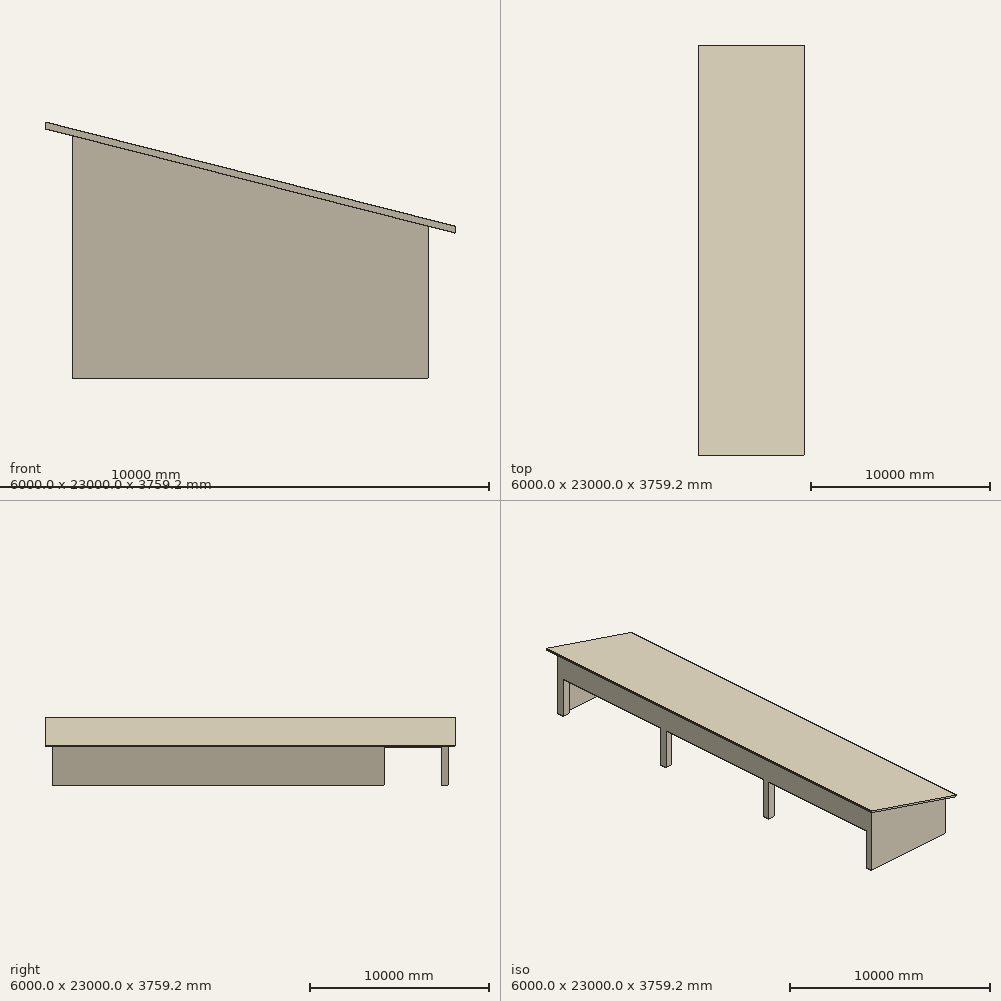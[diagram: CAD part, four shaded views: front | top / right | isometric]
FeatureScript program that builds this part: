
annotation { "Feature Type Name" : "Feature", "Feature Type Description" : "" }
export const myFeature = defineFeature(function(context is Context, id is Id, definition is map)
    precondition{}
    {
        {
            var Q0;
            Q0=qCreatedBy(makeId("Top.planeOp"),FACE);
            var sketch = newSketch(context, id + "F0", { "sketchPlane" : qUnion([Q0])});
            skLineSegment(sketch, "E0.bottom", {"start": v(0, 0) * mm, "end": v(-6000, 0) * mm});
            skLineSegment(sketch, "E0.top", {"start": v(0, 23000) * mm, "end": v(-6000, 23000) * mm});
            skLineSegment(sketch, "E0.left", {"start": v(0, 0) * mm, "end": v(0, 23000) * mm});
            skLineSegment(sketch, "E0.right", {"start": v(-6000, 0) * mm, "end": v(-6000, 23000) * mm});
            skSolve(sketch);
        }
        {
            var Q0;
            Q0=makeQuery(id+"F0.imprint","IMPRINT",FACE,{"disambiguationData":[TD([[makeQuery(id+"F0.imprint","IMPRINT",EDGE,{"derivedFrom":sQuery(id+"F0.wireOp",EDGE,"E0.bottom")}),-1.0]])]});
            extrude(context, id + "F1", {"entities" : qUnion([Q0]), "depth" : 3759.2 * mm, "offsetDistance" : 25 * mm});
        }
        {
            var Q0;
            Q0=makeQuery(id+"F1.opExtrude","SWEPT_FACE",FACE,{"disambiguationData":[OSD([sQuery(id+"F0.wireOp",EDGE,"E0.bottom")])]});
            var sketch = newSketch(context, id + "F2", { "sketchPlane" : qUnion([Q0])});
            skLineSegment(sketch, "E1", {"start": v(0, 0) * mm, "end": v(0, 2133.6) * mm});
            skLineSegment(sketch, "E2", {"start": v(0, 2133.6) * mm, "end": v(0, 2233.6) * mm});
            skLineSegment(sketch, "E3", {"start": v(0, 2233.6) * mm, "end": v(-6000, 3759.2) * mm});
            skLineSegment(sketch, "E4", {"start": v(-6000, 3759.2) * mm, "end": v(-6000, 3659.2) * mm});
            skLineSegment(sketch, "E5", {"start": v(-6000, 3659.2) * mm, "end": v(0, 2133.6) * mm});
            skLineSegment(sketch, "E6", {"start": v(0, 2133.6) * mm, "end": v(-6000, 2133.6) * mm});
            skLineSegment(sketch, "E7", {"start": v(0, 0) * mm, "end": v(-400, 0) * mm});
            skLineSegment(sketch, "E8", {"start": v(-400, 0) * mm, "end": v(-800, 0) * mm});
            skLineSegment(sketch, "E9", {"start": v(-800, 0) * mm, "end": v(-800, 2133.6) * mm});
            skLineSegment(sketch, "E10", {"start": v(-800, 2133.6) * mm, "end": v(-400, 2133.6) * mm});
            skLineSegment(sketch, "E11", {"start": v(-400, 2133.6) * mm, "end": v(-400, 0) * mm});
            skLineSegment(sketch, "E12", {"start": v(-6000, 0) * mm, "end": v(-5600, 0) * mm});
            skLineSegment(sketch, "E13", {"start": v(-5600, 0) * mm, "end": v(-5200, 0) * mm});
            skLineSegment(sketch, "E14", {"start": v(-5200, 0) * mm, "end": v(-5200, 2133.6) * mm});
            skLineSegment(sketch, "E15", {"start": v(-5200, 2133.6) * mm, "end": v(-5600, 2133.6) * mm});
            skLineSegment(sketch, "E16", {"start": v(-5600, 2133.6) * mm, "end": v(-5600, 0) * mm});
            skSolve(sketch);
        }
        {
            var Q0;
            {var subQ0=sQuery(id+"F2.wireOp",EDGE,"E9");Q0=makeQuery(id+"F2.imprint","IMPRINT",FACE,{"disambiguationData":[TD([[makeQuery(id+"F2.imprint","IMPRINT",EDGE,{"derivedFrom":subQ0}),1.0]])]});}
            var Q1;
            {var subQ0=sQuery(id+"F2.wireOp",EDGE,"E1");Q1=makeQuery(id+"F2.imprint","IMPRINT",FACE,{"disambiguationData":[TD([[makeQuery(id+"F2.imprint","IMPRINT",EDGE,{"derivedFrom":subQ0}),-1.0]])]});}
            var Q2;
            {var subQ4=sQuery(id+"F2.wireOp",EDGE,"E12");Q2=makeQuery(id+"F2.imprint","IMPRINT",FACE,{"disambiguationData":[TD([[makeQuery(id+"F2.imprint","IMPRINT",EDGE,{"derivedFrom":subQ4}),-1.0]])]});}
            var Q3;
            {var subQ0=sQuery(id+"F2.wireOp",EDGE,"E3");Q3=makeQuery(id+"F2.imprint","IMPRINT",FACE,{"disambiguationData":[TD([[makeQuery(id+"F2.imprint","IMPRINT",EDGE,{"derivedFrom":subQ0}),-1.0]])]});}
            extrude(context, id + "F3", {"entities" : qUnion([Q0, Q1, Q2, Q3]), "operationType" : NewBodyOperationType.REMOVE, "oppositeDirection" : true, "depth" : 22800 * mm, "offsetDistance" : 25 * mm});
        }
        {
            var Q0;
            Q0=makeQuery(id+"F3.boolean.opBoolean","COPY",FACE,{"derivedFrom":makeQuery(id+"F3.opExtrude","CAP_FACE",FACE,{"disambiguationData":[OSD([sQuery(id+"F0.wireOp",EDGE,"E0.bottom"),sQuery(id+"F0.wireOp",EDGE,"E0.left"),sQuery(id+"F2.wireOp",EDGE,"E3")])],"isStart":false})});
            var Q1;
            Q1=makeQuery(id+"F3.boolean.opBoolean","COPY",FACE,{"derivedFrom":makeQuery(id+"F3.opExtrude","CAP_FACE",FACE,{"disambiguationData":[OSD([sQuery(id+"F0.wireOp",EDGE,"E0.bottom"),sQuery(id+"F0.wireOp",EDGE,"E0.right"),sQuery(id+"F2.wireOp",EDGE,"E6"),sQuery(id+"F2.wireOp",EDGE,"E12"),sQuery(id+"F2.wireOp",EDGE,"E16")])],"isStart":false})});
            var Q2;
            Q2=makeQuery(id+"F3.boolean.opBoolean","COPY",FACE,{"derivedFrom":makeQuery(id+"F3.opExtrude","CAP_FACE",FACE,{"disambiguationData":[OSD([sQuery(id+"F2.wireOp",EDGE,"E1"),sQuery(id+"F2.wireOp",EDGE,"E6"),sQuery(id+"F2.wireOp",EDGE,"E7"),sQuery(id+"F2.wireOp",EDGE,"E11")])],"isStart":false})});
            extrude(context, id + "F4", {"entities" : qUnion([Q0, Q1, Q2]), "operationType" : NewBodyOperationType.REMOVE, "oppositeDirection" : true, "depth" : 200 * mm, "offsetDistance" : 25 * mm});
        }
        {
            var Q0;
            {var subQ0=sQuery(id+"F2.wireOp",EDGE,"E11");Q0=makeQuery(id+"F4.boolean.opBoolean","MERGE",FACE,{"derivedFrom":[makeQuery(id+"F3.boolean.opBoolean","COPY",FACE,{"derivedFrom":makeQuery(id+"F3.opExtrude","SWEPT_FACE",FACE,{"disambiguationData":[OSD([subQ0])]})})],"fromTools":[makeQuery(id+"F4.opExtrude","SWEPT_FACE",FACE,{"disambiguationData":[OSD([subQ0])]})]});}
            var sketch = newSketch(context, id + "F5", { "sketchPlane" : qUnion([Q0])});
            skLineSegment(sketch, "E17", {"start": v(0, 0) * mm, "end": v(400, 0) * mm});
            skLineSegment(sketch, "E18", {"start": v(400, 0) * mm, "end": v(800, 0) * mm});
            skLineSegment(sketch, "E19", {"start": v(800, 0) * mm, "end": v(800, 2133.6) * mm});
            skLineSegment(sketch, "E20", {"start": v(800, 2133.6) * mm, "end": v(400, 2133.6) * mm});
            skLineSegment(sketch, "E21", {"start": v(400, 2133.6) * mm, "end": v(400, 0) * mm});
            skLineSegment(sketch, "E22", {"start": v(23000, 0) * mm, "end": v(22600, 0) * mm});
            skLineSegment(sketch, "E23", {"start": v(22600, 0) * mm, "end": v(22200, 0) * mm});
            skLineSegment(sketch, "E24", {"start": v(22200, 0) * mm, "end": v(22200, 2133.6) * mm});
            skLineSegment(sketch, "E25", {"start": v(22200, 2133.6) * mm, "end": v(22600, 2133.6) * mm});
            skLineSegment(sketch, "E26", {"start": v(22600, 2133.6) * mm, "end": v(22600, 0) * mm});
            skLineSegment(sketch, "E27", {"start": v(800, 0) * mm, "end": v(7670, 0) * mm});
            skLineSegment(sketch, "E28", {"start": v(7670, 0) * mm, "end": v(8070, 0) * mm});
            skLineSegment(sketch, "E29", {"start": v(8070, 0) * mm, "end": v(14940, 0) * mm});
            skLineSegment(sketch, "E30", {"start": v(14940, 0) * mm, "end": v(15340, 0) * mm});
            skLineSegment(sketch, "E31", {"start": v(15340, 0) * mm, "end": v(22200, 0) * mm});
            skLineSegment(sketch, "E32", {"start": v(7670, 0) * mm, "end": v(7670, 2133.6) * mm});
            skLineSegment(sketch, "E33", {"start": v(8070, 0) * mm, "end": v(8070, 2133.6) * mm});
            skLineSegment(sketch, "E34", {"start": v(14940, 0) * mm, "end": v(14940, 2133.6) * mm});
            skLineSegment(sketch, "E35", {"start": v(15340, 0) * mm, "end": v(15340, 2133.6) * mm});
            skSolve(sketch);
        }
        {
            var Q0;
            Q0=makeQuery(id+"F5.imprint","IMPRINT",FACE,{"disambiguationData":[TD([[makeQuery(id+"F5.imprint","IMPRINT",EDGE,{"derivedFrom":sQuery(id+"F5.wireOp",EDGE,"E17")}),-1.0]])]});
            var Q1;
            Q1=makeQuery(id+"F5.imprint","IMPRINT",FACE,{"disambiguationData":[TD([[makeQuery(id+"F5.imprint","IMPRINT",EDGE,{"derivedFrom":sQuery(id+"F5.wireOp",EDGE,"E22")}),-1.0]])]});
            var Q2;
            {var subQ0=sQuery(id+"F5.wireOp",EDGE,"E19");Q2=makeQuery(id+"F5.imprint","IMPRINT",FACE,{"disambiguationData":[TD([[makeQuery(id+"F5.imprint","IMPRINT",EDGE,{"derivedFrom":subQ0}),-1.0]])]});}
            var Q3;
            Q3=makeQuery(id+"F5.imprint","IMPRINT",FACE,{"disambiguationData":[TD([[makeQuery(id+"F5.imprint","IMPRINT",EDGE,{"derivedFrom":sQuery(id+"F5.wireOp",EDGE,"E29")}),-1.0]])]});
            var Q4;
            {var subQ0=sQuery(id+"F5.wireOp",EDGE,"E24");Q4=makeQuery(id+"F5.imprint","IMPRINT",FACE,{"disambiguationData":[TD([[makeQuery(id+"F5.imprint","IMPRINT",EDGE,{"derivedFrom":subQ0}),1.0]])]});}
            extrude(context, id + "F6", {"entities" : qUnion([Q0, Q1, Q2, Q3, Q4]), "operationType" : NewBodyOperationType.REMOVE, "oppositeDirection" : true, "depth" : 6000 * mm, "offsetDistance" : 25 * mm});
        }
        {
            var Q0;
            {var subQ0=sQuery(id+"F2.wireOp",EDGE,"E11");var subQ5=sQuery(id+"F5.wireOp",EDGE,"E19");Q0=makeQuery(id+"F6.boolean.opBoolean","SPLIT",FACE,{"disambiguationData":[TD([makeQuery(id+"F6.opExtrude","SWEPT_FACE",FACE,{"disambiguationData":[OSD([subQ5])]})])],"derivedFrom":makeQuery(id+"F4.boolean.opBoolean","MERGE",FACE,{"derivedFrom":[makeQuery(id+"F3.boolean.opBoolean","COPY",FACE,{"derivedFrom":makeQuery(id+"F3.opExtrude","SWEPT_FACE",FACE,{"disambiguationData":[OSD([subQ0])]})})],"fromTools":[makeQuery(id+"F4.opExtrude","SWEPT_FACE",FACE,{"disambiguationData":[OSD([subQ0])]})]})});}
            var sketch = newSketch(context, id + "F7", { "sketchPlane" : qUnion([Q0])});
            skLineSegment(sketch, "E36", {"start": v(800, 2133.6) * mm, "end": v(22216.48, 2133.6) * mm});
            skLineSegment(sketch, "E37", {"start": v(22216.48, 2133.6) * mm, "end": v(22216.48, 0) * mm});
            skLineSegment(sketch, "E38", {"start": v(22216.48, 0) * mm, "end": v(800, 0) * mm});
            skLineSegment(sketch, "E39", {"start": v(800, 0) * mm, "end": v(800, 2133.6) * mm});
            skSolve(sketch);
        }
        {
            var Q0;
            Q0=makeQuery(id+"F7.imprint","IMPRINT",FACE,{"disambiguationData":[TD([[makeQuery(id+"F7.imprint","IMPRINT",EDGE,{"derivedFrom":sQuery(id+"F7.wireOp",EDGE,"E36")}),-1.0]])]});
            extrude(context, id + "F8", {"entities" : qUnion([Q0]), "operationType" : NewBodyOperationType.ADD, "oppositeDirection" : true, "depth" : 200 * mm, "offsetDistance" : 25 * mm});
        }
        {
            var Q0;
            {var subQ5=sQuery(id+"F5.wireOp",EDGE,"E21");var subQ10=sQuery(id+"F2.wireOp",EDGE,"E14");Q0=makeQuery(id+"F6.boolean.opBoolean","COPY",FACE,{"disambiguationData":[TD([makeQuery(id+"F3.boolean.opBoolean","COPY",FACE,{"derivedFrom":makeQuery(id+"F3.opExtrude","SWEPT_FACE",FACE,{"disambiguationData":[OSD([subQ10])]})})])],"derivedFrom":makeQuery(id+"F6.opExtrude","SWEPT_FACE",FACE,{"disambiguationData":[OSD([subQ5])]})});}
            var sketch = newSketch(context, id + "F9", { "sketchPlane" : qUnion([Q0])});
            skLineSegment(sketch, "E40", {"start": v(-5200, 2133.6) * mm, "end": v(-782.68, 2133.6) * mm});
            skLineSegment(sketch, "E41", {"start": v(-782.68, 2133.6) * mm, "end": v(-782.68, 0) * mm});
            skLineSegment(sketch, "E42", {"start": v(-782.68, 0) * mm, "end": v(-5200, 0) * mm});
            skLineSegment(sketch, "E43", {"start": v(-5200, 0) * mm, "end": v(-5200, 2133.6) * mm});
            skSolve(sketch);
        }
        {
            var Q0;
            Q0=makeQuery(id+"F9.imprint","IMPRINT",FACE,{"disambiguationData":[TD([[makeQuery(id+"F9.imprint","IMPRINT",EDGE,{"derivedFrom":sQuery(id+"F9.wireOp",EDGE,"E40")}),-1.0]])]});
            extrude(context, id + "F10", {"entities" : qUnion([Q0]), "operationType" : NewBodyOperationType.ADD, "oppositeDirection" : true, "depth" : 200 * mm, "offsetDistance" : 25 * mm});
        }
        {
            var Q0;
            {var subQ4=sQuery(id+"F5.wireOp",EDGE,"E26");var subQ7=sQuery(id+"F2.wireOp",EDGE,"E9");Q0=makeQuery(id+"F6.boolean.opBoolean","COPY",FACE,{"disambiguationData":[TD([makeQuery(id+"F3.boolean.opBoolean","COPY",FACE,{"derivedFrom":makeQuery(id+"F3.opExtrude","SWEPT_FACE",FACE,{"disambiguationData":[OSD([subQ7])]})})])],"derivedFrom":makeQuery(id+"F6.opExtrude","SWEPT_FACE",FACE,{"disambiguationData":[OSD([subQ4])]})});}
            var sketch = newSketch(context, id + "F11", { "sketchPlane" : qUnion([Q0])});
            skLineSegment(sketch, "E44", {"start": v(800, 2133.6) * mm, "end": v(5227.5, 2133.6) * mm});
            skLineSegment(sketch, "E45", {"start": v(5227.5, 2133.6) * mm, "end": v(5227.5, 0) * mm});
            skLineSegment(sketch, "E46", {"start": v(5227.5, 0) * mm, "end": v(800, 0) * mm});
            skLineSegment(sketch, "E47", {"start": v(800, 0) * mm, "end": v(800, 2133.6) * mm});
            skSolve(sketch);
        }
        {
            var Q0;
            Q0=makeQuery(id+"F11.imprint","IMPRINT",FACE,{"disambiguationData":[TD([[makeQuery(id+"F11.imprint","IMPRINT",EDGE,{"derivedFrom":sQuery(id+"F11.wireOp",EDGE,"E44")}),-1.0]])]});
            extrude(context, id + "F12", {"entities" : qUnion([Q0]), "operationType" : NewBodyOperationType.ADD, "oppositeDirection" : true, "depth" : 200 * mm, "offsetDistance" : 25 * mm});
        }
        {
            var Q0;
            Q0=makeQuery(id+"F1.opExtrude","SWEPT_FACE",FACE,{"disambiguationData":[OSD([sQuery(id+"F0.wireOp",EDGE,"E0.bottom")])]});
            var sketch = newSketch(context, id + "F13", { "sketchPlane" : qUnion([Q0])});
            skLineSegment(sketch, "E48", {"start": v(0, 2133.6) * mm, "end": v(-6000, 3659.2) * mm});
            skSolve(sketch);
        }
        {
            var Q0;
            {var subQ0=sQuery(id+"F13.wireOp",EDGE,"E48");Q0=makeQuery(id+"F13.imprint","IMPRINT",FACE,{"disambiguationData":[TD([[makeQuery(id+"F13.imprint","IMPRINT",EDGE,{"derivedFrom":subQ0}),1.0]])]});}
            extrude(context, id + "F14", {"entities" : qUnion([Q0]), "operationType" : NewBodyOperationType.REMOVE, "oppositeDirection" : true, "depth" : 400 * mm, "offsetDistance" : 25 * mm});
        }
        {
            var Q0;
            Q0=makeQuery(id+"F1.opExtrude","SWEPT_FACE",FACE,{"disambiguationData":[OSD([sQuery(id+"F0.wireOp",EDGE,"E0.top")])]});
            var sketch = newSketch(context, id + "F15", { "sketchPlane" : qUnion([Q0])});
            skLineSegment(sketch, "E49", {"start": v(6000, 3759.2) * mm, "end": v(6000, 3659.2) * mm});
            skLineSegment(sketch, "E50", {"start": v(6000, 3659.2) * mm, "end": v(0, 2133.6) * mm});
            skLineSegment(sketch, "E51", {"start": v(0, 2133.6) * mm, "end": v(400, 2133.6) * mm});
            skLineSegment(sketch, "E52", {"start": v(400, 2133.6) * mm, "end": v(400, 2235.3) * mm});
            skSolve(sketch);
        }
        {
            var Q0;
            {var subQ4=sQuery(id+"F15.wireOp",EDGE,"E52");Q0=makeQuery(id+"F15.imprint","IMPRINT",FACE,{"disambiguationData":[TD([[makeQuery(id+"F15.imprint","IMPRINT",EDGE,{"derivedFrom":subQ4}),-1.0]])]});}
            extrude(context, id + "F16", {"entities" : qUnion([Q0]), "operationType" : NewBodyOperationType.REMOVE, "oppositeDirection" : true, "depth" : 400 * mm, "offsetDistance" : 25 * mm});
        }
        {
            var Q0;
            {var subQ0=sQuery(id+"F15.wireOp",EDGE,"E51");Q0=makeQuery(id+"F15.imprint","IMPRINT",FACE,{"disambiguationData":[TD([[makeQuery(id+"F15.imprint","IMPRINT",EDGE,{"derivedFrom":subQ0}),1.0]])]});}
            extrude(context, id + "F17", {"entities" : qUnion([Q0]), "operationType" : NewBodyOperationType.REMOVE, "oppositeDirection" : true, "depth" : 23000 * mm, "offsetDistance" : 25 * mm});
        }
        {
            var Q0;
            {var subQ0=sQuery(id+"F2.wireOp",EDGE,"E11");var subQ1=sQuery(id+"F2.wireOp",EDGE,"E10");var subQ2=sQuery(id+"F2.wireOp",EDGE,"E6");var subQ3=sQuery(id+"F0.wireOp",EDGE,"E0.right");var subQ4=sQuery(id+"F0.wireOp",EDGE,"E0.bottom");var subQ8=sQuery(id+"F5.wireOp",EDGE,"E21");var subQ13=sQuery(id+"F2.wireOp",EDGE,"E14");var subQ17=sQuery(id+"F2.wireOp",EDGE,"E9");var subQ22=makeQuery(id+"F6.opExtrude","SWEPT_FACE",FACE,{"disambiguationData":[OSD([subQ8])]});Q0=makeQuery(id+"F14.boolean.opBoolean","MERGE",FACE,{"derivedFrom":[makeQuery(id+"F10.boolean.opBoolean","MERGE",FACE,{"derivedFrom":[makeQuery(id+"F6.boolean.opBoolean","COPY",FACE,{"disambiguationData":[TD([makeQuery(id+"F3.boolean.opBoolean","COPY",FACE,{"derivedFrom":makeQuery(id+"F3.opExtrude","SWEPT_FACE",FACE,{"disambiguationData":[OSD([subQ17])]})})])],"derivedFrom":subQ22}),makeQuery(id+"F6.boolean.opBoolean","COPY",FACE,{"disambiguationData":[TD([makeQuery(id+"F3.boolean.opBoolean","COPY",FACE,{"derivedFrom":makeQuery(id+"F3.opExtrude","SWEPT_FACE",FACE,{"disambiguationData":[OSD([subQ13])]})})])],"derivedFrom":subQ22}),makeQuery(id+"F10.opExtrude","CAP_FACE",FACE,{"disambiguationData":[OSD([sQuery(id+"F9.wireOp",EDGE,"E40"),sQuery(id+"F9.wireOp",EDGE,"E41"),sQuery(id+"F9.wireOp",EDGE,"E42"),sQuery(id+"F9.wireOp",EDGE,"E43")])],"isStart":true})]})],"fromTools":[makeQuery(id+"F14.opExtrude","CAP_FACE",FACE,{"disambiguationData":[OSD([subQ4,subQ3,subQ2,subQ1,subQ0,sQuery(id+"F13.wireOp",EDGE,"E48")])],"isStart":false})]});}
            var sketch = newSketch(context, id + "F18", { "sketchPlane" : qUnion([Q0])});
            skLineSegment(sketch, "E53", {"start": v(-5600, 2133.6) * mm, "end": v(-5600, 3557.5) * mm});
            skSolve(sketch);
        }
        {
            var Q0;
            {var subQ0=sQuery(id+"F18.wireOp",EDGE,"E53");Q0=makeQuery(id+"F18.imprint","IMPRINT",FACE,{"disambiguationData":[TD([[makeQuery(id+"F18.imprint","IMPRINT",EDGE,{"derivedFrom":subQ0}),1.0]])]});}
            extrude(context, id + "F19", {"entities" : qUnion([Q0]), "operationType" : NewBodyOperationType.REMOVE, "oppositeDirection" : true, "depth" : 23000 * mm, "offsetDistance" : 25 * mm});
        }
        {
            var Q0;
            {var subQ0=sQuery(id+"F2.wireOp",EDGE,"E11");var subQ1=sQuery(id+"F2.wireOp",EDGE,"E10");var subQ2=sQuery(id+"F2.wireOp",EDGE,"E6");var subQ3=sQuery(id+"F0.wireOp",EDGE,"E0.right");var subQ4=sQuery(id+"F0.wireOp",EDGE,"E0.bottom");var subQ8=sQuery(id+"F5.wireOp",EDGE,"E21");var subQ13=sQuery(id+"F2.wireOp",EDGE,"E14");var subQ17=sQuery(id+"F2.wireOp",EDGE,"E9");var subQ22=makeQuery(id+"F6.opExtrude","SWEPT_FACE",FACE,{"disambiguationData":[OSD([subQ8])]});Q0=makeQuery(id+"F14.boolean.opBoolean","MERGE",FACE,{"derivedFrom":[makeQuery(id+"F10.boolean.opBoolean","MERGE",FACE,{"derivedFrom":[makeQuery(id+"F6.boolean.opBoolean","COPY",FACE,{"disambiguationData":[TD([makeQuery(id+"F3.boolean.opBoolean","COPY",FACE,{"derivedFrom":makeQuery(id+"F3.opExtrude","SWEPT_FACE",FACE,{"disambiguationData":[OSD([subQ17])]})})])],"derivedFrom":subQ22}),makeQuery(id+"F6.boolean.opBoolean","COPY",FACE,{"disambiguationData":[TD([makeQuery(id+"F3.boolean.opBoolean","COPY",FACE,{"derivedFrom":makeQuery(id+"F3.opExtrude","SWEPT_FACE",FACE,{"disambiguationData":[OSD([subQ13])]})})])],"derivedFrom":subQ22}),makeQuery(id+"F10.opExtrude","CAP_FACE",FACE,{"disambiguationData":[OSD([sQuery(id+"F9.wireOp",EDGE,"E40"),sQuery(id+"F9.wireOp",EDGE,"E41"),sQuery(id+"F9.wireOp",EDGE,"E42"),sQuery(id+"F9.wireOp",EDGE,"E43")])],"isStart":true})]})],"fromTools":[makeQuery(id+"F14.opExtrude","CAP_FACE",FACE,{"disambiguationData":[OSD([subQ4,subQ3,subQ2,subQ1,subQ0,sQuery(id+"F13.wireOp",EDGE,"E48")])],"isStart":false})]});}
            var sketch = newSketch(context, id + "F20", { "sketchPlane" : qUnion([Q0])});
            skLineSegment(sketch, "E54", {"start": v(-400, 0) * mm, "end": v(-800, 0) * mm});
            skLineSegment(sketch, "E55", {"start": v(-800, 0) * mm, "end": v(-800, 2337.01) * mm});
            skLineSegment(sketch, "E56", {"start": v(-5600, 0) * mm, "end": v(-5200, 0) * mm});
            skLineSegment(sketch, "E57", {"start": v(-5200, 0) * mm, "end": v(-5200, 3455.79) * mm});
            skLineSegment(sketch, "E58", {"start": v(-5200, 0) * mm, "end": v(-5200, 2133.6) * mm});
            skLineSegment(sketch, "E59", {"start": v(-5200, 2133.6) * mm, "end": v(-800, 2133.6) * mm});
            skSolve(sketch);
        }
        {
            var Q0;
            {var subQ4=sQuery(id+"F20.wireOp",EDGE,"E57");Q0=makeQuery(id+"F20.imprint","IMPRINT",FACE,{"disambiguationData":[TD([[makeQuery(id+"F20.imprint","IMPRINT",EDGE,{"derivedFrom":subQ4}),-1.0]])]});}
            extrude(context, id + "F21", {"entities" : qUnion([Q0]), "operationType" : NewBodyOperationType.REMOVE, "oppositeDirection" : true, "depth" : 22000 * mm, "offsetDistance" : 25 * mm});
        }
        {
            var Q0;
            {var subQ4=sQuery(id+"F20.wireOp",EDGE,"E57");Q0=makeQuery(id+"F20.imprint","IMPRINT",FACE,{"disambiguationData":[TD([[makeQuery(id+"F20.imprint","IMPRINT",EDGE,{"derivedFrom":subQ4}),-1.0]])]});}
            extrude(context, id + "F22", {"entities" : qUnion([Q0]), "operationType" : NewBodyOperationType.ADD, "oppositeDirection" : true, "depth" : 200 * mm, "offsetDistance" : 25 * mm});
        }
        {
            var Q0;
            {var subQ0=sQuery(id+"F2.wireOp",EDGE,"E11");var subQ11=sQuery(id+"F5.wireOp",EDGE,"E34");var subQ15=sQuery(id+"F5.wireOp",EDGE,"E19");var subQ16=sQuery(id+"F5.wireOp",EDGE,"E32");var subQ19=sQuery(id+"F5.wireOp",EDGE,"E24");var subQ26=makeQuery(id+"F4.boolean.opBoolean","MERGE",FACE,{"derivedFrom":[makeQuery(id+"F3.boolean.opBoolean","COPY",FACE,{"derivedFrom":makeQuery(id+"F3.opExtrude","SWEPT_FACE",FACE,{"disambiguationData":[OSD([subQ0])]})})],"fromTools":[makeQuery(id+"F4.opExtrude","SWEPT_FACE",FACE,{"disambiguationData":[OSD([subQ0])]})]});Q0=makeQuery(id+"F17.boolean.opBoolean","MERGE",FACE,{"derivedFrom":[makeQuery(id+"F8.boolean.opBoolean","MERGE",FACE,{"derivedFrom":[makeQuery(id+"F6.boolean.opBoolean","SPLIT",FACE,{"disambiguationData":[TD([makeQuery(id+"F6.opExtrude","SWEPT_FACE",FACE,{"disambiguationData":[OSD([subQ15])]})])],"derivedFrom":subQ26}),makeQuery(id+"F6.boolean.opBoolean","SPLIT",FACE,{"disambiguationData":[TD([makeQuery(id+"F6.opExtrude","SWEPT_FACE",FACE,{"disambiguationData":[OSD([subQ19])]})])],"derivedFrom":subQ26}),makeQuery(id+"F6.boolean.opBoolean","SPLIT",FACE,{"disambiguationData":[TD([makeQuery(id+"F6.opExtrude","SWEPT_FACE",FACE,{"disambiguationData":[OSD([subQ16])]})])],"derivedFrom":subQ26}),makeQuery(id+"F6.boolean.opBoolean","SPLIT",FACE,{"disambiguationData":[TD([makeQuery(id+"F6.opExtrude","SWEPT_FACE",FACE,{"disambiguationData":[OSD([subQ11])]})])],"derivedFrom":subQ26}),makeQuery(id+"F8.opExtrude","CAP_FACE",FACE,{"disambiguationData":[OSD([sQuery(id+"F7.wireOp",EDGE,"E36"),sQuery(id+"F7.wireOp",EDGE,"E37"),sQuery(id+"F7.wireOp",EDGE,"E38"),sQuery(id+"F7.wireOp",EDGE,"E39")])],"isStart":true})]})],"fromTools":[makeQuery(id+"F17.opExtrude","SWEPT_FACE",FACE,{"disambiguationData":[OSD([sQuery(id+"F15.wireOp",EDGE,"E52")])]})]});}
            var sketch = newSketch(context, id + "F23", { "sketchPlane" : qUnion([Q0])});
            skLineSegment(sketch, "E60", {"start": v(22600, 0) * mm, "end": v(22200, 0) * mm});
            skLineSegment(sketch, "E61", {"start": v(22200, 0) * mm, "end": v(22200, 2113.6) * mm});
            skLineSegment(sketch, "E62", {"start": v(22200, 2113.6) * mm, "end": v(19000, 2113.6) * mm});
            skLineSegment(sketch, "E63", {"start": v(19000, 2113.6) * mm, "end": v(19000, 0) * mm});
            skLineSegment(sketch, "E64", {"start": v(19000, 0) * mm, "end": v(22200, 0) * mm});
            skSolve(sketch);
        }
        {
            var Q0;
            Q0=makeQuery(id+"F23.imprint","IMPRINT",FACE,{"disambiguationData":[TD([[makeQuery(id+"F23.imprint","IMPRINT",EDGE,{"derivedFrom":sQuery(id+"F23.wireOp",EDGE,"E61")}),1.0]])]});
            extrude(context, id + "F24", {"entities" : qUnion([Q0]), "operationType" : NewBodyOperationType.REMOVE, "oppositeDirection" : true, "depth" : 200 * mm, "offsetDistance" : 25 * mm});
        }
    });
